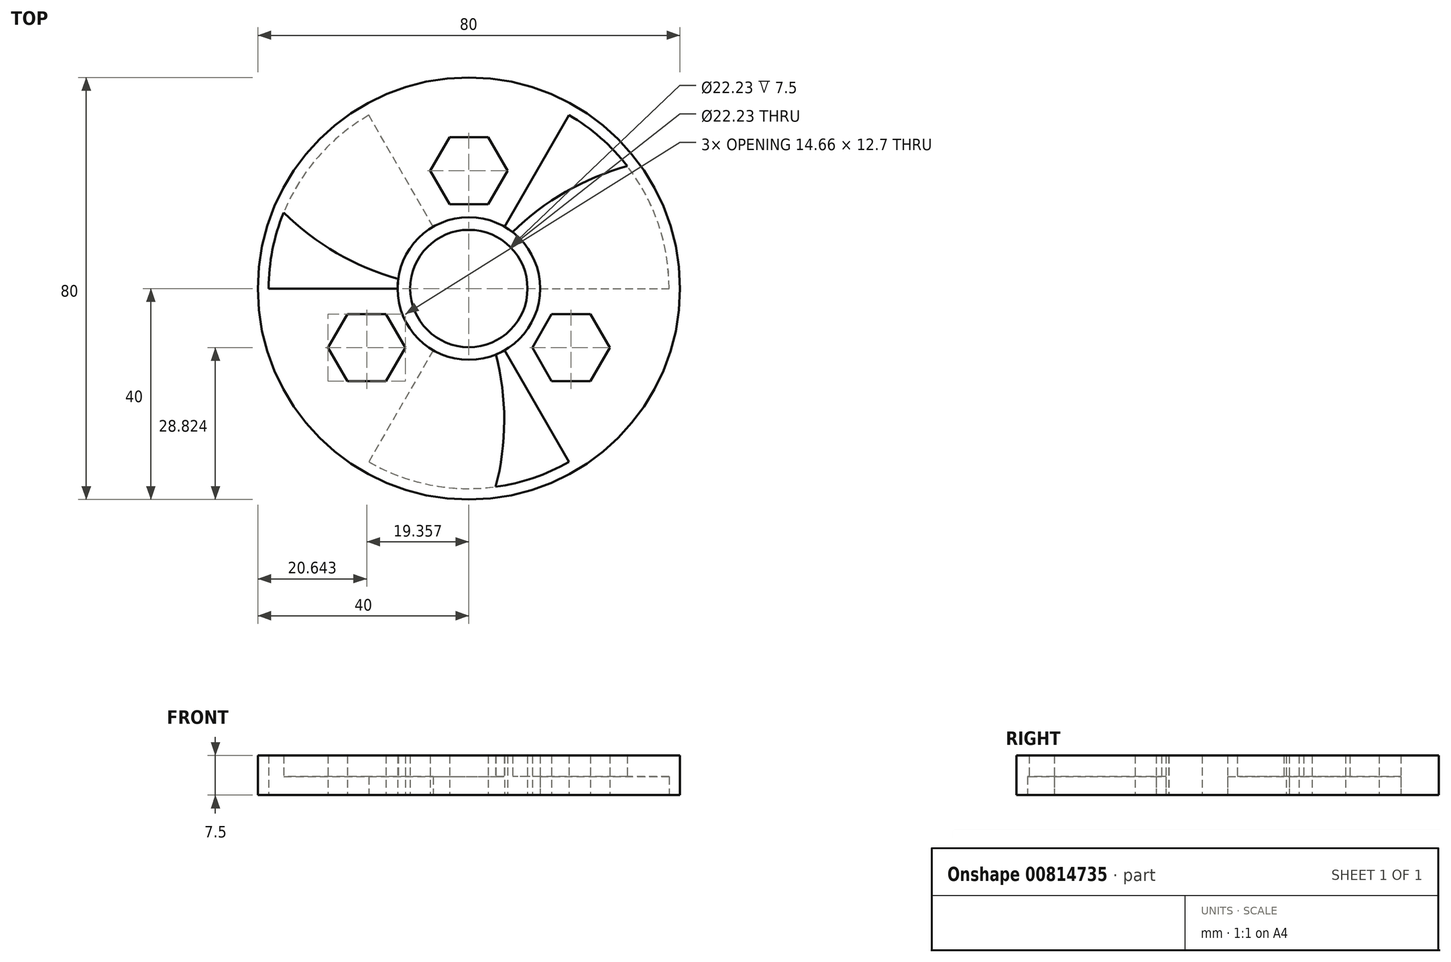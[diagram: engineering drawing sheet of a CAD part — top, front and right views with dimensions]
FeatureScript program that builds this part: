
annotation { "Feature Type Name" : "Feature", "Feature Type Description" : "" }
export const myFeature = defineFeature(function(context is Context, id is Id, definition is map)
    precondition{}
    {
        {
            var Q0;
            Q0=qCreatedBy(makeId("Top.planeOp"),FACE);
            var sketch = newSketch(context, id + "F0", { "sketchPlane" : qUnion([Q0])});
            skCircle(sketch, "E0", {"center": v(0, 0) * mm, "radius": 40 * mm});
            skCircle(sketch, "E1", {"center": v(0, 0) * mm, "radius": 11.11 * mm});
            skCircle(sketch, "E2.cCircle", {"center": v(0, 22.35) * mm, "radius": 6.35 * mm, "construction": true});
            skLineSegment(sketch, "E2.0", {"start": v(3.67, 16) * mm, "end": v(-3.67, 16) * mm});
            skLineSegment(sketch, "E2.1", {"start": v(-3.67, 16) * mm, "end": v(-7.33, 22.35) * mm});
            skLineSegment(sketch, "E2.2", {"start": v(-7.33, 22.35) * mm, "end": v(-3.67, 28.7) * mm});
            skLineSegment(sketch, "E2.3", {"start": v(-3.67, 28.7) * mm, "end": v(3.67, 28.7) * mm});
            skLineSegment(sketch, "E2.4", {"start": v(3.67, 28.7) * mm, "end": v(7.33, 22.35) * mm});
            skLineSegment(sketch, "E2.5", {"start": v(7.33, 22.35) * mm, "end": v(3.67, 16) * mm});
            skPoint(sketch, "E2.0.midPoint", {"position": v(0, 16) * mm});
            skCircle(sketch, "E3.1.0", {"center": v(-19.36, -11.18) * mm, "radius": 6.35 * mm, "construction": true});
            skCircle(sketch, "E3.2.0", {"center": v(19.36, -11.18) * mm, "radius": 6.35 * mm, "construction": true});
            skLineSegment(sketch, "E4.0", {"start": v(-15.7, -17.53) * mm, "end": v(-23.02, -17.53) * mm});
            skLineSegment(sketch, "E4.1", {"start": v(-23.02, -17.53) * mm, "end": v(-26.69, -11.18) * mm});
            skLineSegment(sketch, "E4.2", {"start": v(-26.69, -11.18) * mm, "end": v(-23.02, -4.83) * mm});
            skLineSegment(sketch, "E4.3", {"start": v(-23.02, -4.83) * mm, "end": v(-15.7, -4.83) * mm});
            skLineSegment(sketch, "E4.4", {"start": v(-15.7, -4.83) * mm, "end": v(-12.03, -11.18) * mm});
            skLineSegment(sketch, "E4.5", {"start": v(-12.03, -11.18) * mm, "end": v(-15.7, -17.53) * mm});
            skPoint(sketch, "E4.0.midPoint", {"position": v(-19.36, -17.53) * mm});
            skLineSegment(sketch, "E5.0", {"start": v(23.02, -17.53) * mm, "end": v(15.7, -17.53) * mm});
            skLineSegment(sketch, "E5.1", {"start": v(15.7, -17.53) * mm, "end": v(12.03, -11.18) * mm});
            skLineSegment(sketch, "E5.2", {"start": v(12.03, -11.18) * mm, "end": v(15.7, -4.83) * mm});
            skLineSegment(sketch, "E5.3", {"start": v(15.7, -4.83) * mm, "end": v(23.02, -4.83) * mm});
            skLineSegment(sketch, "E5.4", {"start": v(23.02, -4.83) * mm, "end": v(26.69, -11.18) * mm});
            skLineSegment(sketch, "E5.5", {"start": v(26.69, -11.18) * mm, "end": v(23.02, -17.53) * mm});
            skPoint(sketch, "E5.0.midPoint", {"position": v(19.36, -17.53) * mm});
            skLineSegment(sketch, "E6", {"start": v(0, 0) * mm, "end": v(-20, 34.64) * mm});
            skLineSegment(sketch, "E7", {"start": v(0, 0) * mm, "end": v(-40, 0) * mm});
            skLineSegment(sketch, "E8", {"start": v(0, 0) * mm, "end": v(-19.36, -11.18) * mm});
            skLineSegment(sketch, "E9", {"start": v(0, 0) * mm, "end": v(19.36, -11.18) * mm});
            skLineSegment(sketch, "E10.1.0", {"start": v(0, 0) * mm, "end": v(20, -34.64) * mm});
            skLineSegment(sketch, "E10.1.1", {"start": v(0, 0) * mm, "end": v(-20, -34.64) * mm});
            skLineSegment(sketch, "E10.2.0", {"start": v(0, 0) * mm, "end": v(20, 34.64) * mm});
            skLineSegment(sketch, "E10.2.1", {"start": v(0, 0) * mm, "end": v(40, 0) * mm});
            skArc(sketch, "E11", {"start": v(-36.66, 16) * mm, "mid": v(-20, 4.17) * mm, "end": v(0, 0) * mm});
            skArc(sketch, "E12.1.0", {"start": v(4.47, -39.75) * mm, "mid": v(6.38, -19.4) * mm, "end": v(0, 0) * mm});
            skArc(sketch, "E12.2.0", {"start": v(32.19, 23.75) * mm, "mid": v(13.62, 15.23) * mm, "end": v(0, 0) * mm});
            skCircle(sketch, "E13", {"center": v(0, 0) * mm, "radius": 13.51 * mm});
            skCircle(sketch, "E14", {"center": v(0, 0) * mm, "radius": 37.93 * mm});
            skSolve(sketch);
        }
        {
            var Q0;
            Q0 = qSketchRegion(id + "F0", true);
            var Q1;
            Q1=makeQuery(id+"F0.imprint","IMPRINT",FACE,{"disambiguationData":[TD([[makeQuery(id+"F0.imprint","IMPRINT",EDGE,{"derivedFrom":sQuery(id+"F0.wireOp",EDGE,"E4.0")}),1.0]])]});
            var Q2;
            {var subQ0=sQuery(id+"F0.wireOp",EDGE,"E13");var subQ1=sQuery(id+"F0.wireOp",EDGE,"E10.1.1");var subQ2=makeQuery(id+"F0.imprint","INTERSECT",VERTEX,{"derivedFrom":[subQ1,subQ0]});Q2=makeQuery(id+"F0.imprint","IMPRINT",FACE,{"disambiguationData":[TD([[makeQuery(id+"F0.imprint","IMPRINT",EDGE,{"disambiguationData":[TD([[subQ2,-1.0]])],"derivedFrom":subQ1}),1.0]])]});}
            var Q3;
            {var subQ0=sQuery(id+"F0.wireOp",EDGE,"E13");var subQ1=sQuery(id+"F0.wireOp",EDGE,"E10.1.0");var subQ2=makeQuery(id+"F0.imprint","INTERSECT",VERTEX,{"derivedFrom":[subQ1,subQ0]});Q3=makeQuery(id+"F0.imprint","IMPRINT",FACE,{"disambiguationData":[TD([[makeQuery(id+"F0.imprint","IMPRINT",EDGE,{"disambiguationData":[TD([[subQ2,-1.0]])],"derivedFrom":subQ1}),-1.0]])]});}
            var Q4;
            Q4=makeQuery(id+"F0.imprint","IMPRINT",FACE,{"disambiguationData":[TD([[makeQuery(id+"F0.imprint","IMPRINT",EDGE,{"derivedFrom":sQuery(id+"F0.wireOp",EDGE,"E5.0")}),1.0]])]});
            var Q5;
            {var subQ0=sQuery(id+"F0.wireOp",EDGE,"E8");var subQ1=sQuery(id+"F0.wireOp",EDGE,"E1");var subQ2=makeQuery(id+"F0.imprint","INTERSECT",VERTEX,{"derivedFrom":[subQ1,subQ0]});Q5=makeQuery(id+"F0.imprint","IMPRINT",FACE,{"disambiguationData":[TD([[makeQuery(id+"F0.imprint","IMPRINT",EDGE,{"disambiguationData":[TD([[subQ2,-1.0]])],"derivedFrom":subQ1}),-1.0]])]});}
            var Q6;
            {var subQ0=sQuery(id+"F0.wireOp",EDGE,"E7");var subQ1=sQuery(id+"F0.wireOp",EDGE,"E1");var subQ2=makeQuery(id+"F0.imprint","INTERSECT",VERTEX,{"derivedFrom":[subQ1,subQ0]});Q6=makeQuery(id+"F0.imprint","IMPRINT",FACE,{"disambiguationData":[TD([[makeQuery(id+"F0.imprint","IMPRINT",EDGE,{"disambiguationData":[TD([[subQ2,-1.0]])],"derivedFrom":subQ1}),-1.0]])]});}
            var Q7;
            {var subQ0=sQuery(id+"F0.wireOp",EDGE,"E6");var subQ1=sQuery(id+"F0.wireOp",EDGE,"E1");var subQ2=makeQuery(id+"F0.imprint","INTERSECT",VERTEX,{"derivedFrom":[subQ1,subQ0]});Q7=makeQuery(id+"F0.imprint","IMPRINT",FACE,{"disambiguationData":[TD([[makeQuery(id+"F0.imprint","IMPRINT",EDGE,{"disambiguationData":[TD([[subQ2,-1.0]])],"derivedFrom":subQ1}),-1.0]])]});}
            var Q8;
            {var subQ0=sQuery(id+"F0.wireOp",EDGE,"E13");var subQ1=sQuery(id+"F0.wireOp",EDGE,"E7");var subQ2=makeQuery(id+"F0.imprint","INTERSECT",VERTEX,{"derivedFrom":[subQ1,subQ0]});Q8=makeQuery(id+"F0.imprint","IMPRINT",FACE,{"disambiguationData":[TD([[makeQuery(id+"F0.imprint","IMPRINT",EDGE,{"disambiguationData":[TD([[subQ2,-1.0]])],"derivedFrom":subQ1}),-1.0]])]});}
            var Q9;
            {var subQ0=sQuery(id+"F0.wireOp",EDGE,"E13");var subQ1=sQuery(id+"F0.wireOp",EDGE,"E6");var subQ2=makeQuery(id+"F0.imprint","INTERSECT",VERTEX,{"derivedFrom":[subQ1,subQ0]});Q9=makeQuery(id+"F0.imprint","IMPRINT",FACE,{"disambiguationData":[TD([[makeQuery(id+"F0.imprint","IMPRINT",EDGE,{"disambiguationData":[TD([[subQ2,-1.0]])],"derivedFrom":subQ1}),1.0]])]});}
            var Q10;
            Q10=makeQuery(id+"F0.imprint","IMPRINT",FACE,{"disambiguationData":[TD([[makeQuery(id+"F0.imprint","IMPRINT",EDGE,{"derivedFrom":sQuery(id+"F0.wireOp",EDGE,"E2.0")}),1.0]])]});
            var Q11;
            {var subQ0=sQuery(id+"F0.wireOp",EDGE,"E10.2.0");var subQ1=sQuery(id+"F0.wireOp",EDGE,"E1");var subQ2=makeQuery(id+"F0.imprint","INTERSECT",VERTEX,{"derivedFrom":[subQ1,subQ0]});Q11=makeQuery(id+"F0.imprint","IMPRINT",FACE,{"disambiguationData":[TD([[makeQuery(id+"F0.imprint","IMPRINT",EDGE,{"disambiguationData":[TD([[subQ2,-1.0]])],"derivedFrom":subQ1}),-1.0]])]});}
            var Q12;
            {var subQ0=sQuery(id+"F0.wireOp",EDGE,"E11");var subQ1=sQuery(id+"F0.wireOp",EDGE,"E1");var subQ2=makeQuery(id+"F0.imprint","INTERSECT",VERTEX,{"derivedFrom":[subQ1,subQ0]});Q12=makeQuery(id+"F0.imprint","IMPRINT",FACE,{"disambiguationData":[TD([[makeQuery(id+"F0.imprint","IMPRINT",EDGE,{"disambiguationData":[TD([[subQ2,-1.0]])],"derivedFrom":subQ1}),-1.0]])]});}
            var Q13;
            {var subQ0=sQuery(id+"F0.wireOp",EDGE,"E12.2.0");var subQ1=sQuery(id+"F0.wireOp",EDGE,"E1");var subQ2=makeQuery(id+"F0.imprint","INTERSECT",VERTEX,{"derivedFrom":[subQ1,subQ0]});Q13=makeQuery(id+"F0.imprint","IMPRINT",FACE,{"disambiguationData":[TD([[makeQuery(id+"F0.imprint","IMPRINT",EDGE,{"disambiguationData":[TD([[subQ2,1.0]])],"derivedFrom":subQ1}),-1.0]])]});}
            var Q14;
            {var subQ0=sQuery(id+"F0.wireOp",EDGE,"E12.2.0");var subQ1=sQuery(id+"F0.wireOp",EDGE,"E1");var subQ2=makeQuery(id+"F0.imprint","INTERSECT",VERTEX,{"derivedFrom":[subQ1,subQ0]});Q14=makeQuery(id+"F0.imprint","IMPRINT",FACE,{"disambiguationData":[TD([[makeQuery(id+"F0.imprint","IMPRINT",EDGE,{"disambiguationData":[TD([[subQ2,-1.0]])],"derivedFrom":subQ1}),-1.0]])]});}
            var Q15;
            {var subQ0=sQuery(id+"F0.wireOp",EDGE,"E10.1.0");var subQ1=sQuery(id+"F0.wireOp",EDGE,"E1");var subQ2=makeQuery(id+"F0.imprint","INTERSECT",VERTEX,{"derivedFrom":[subQ1,subQ0]});Q15=makeQuery(id+"F0.imprint","IMPRINT",FACE,{"disambiguationData":[TD([[makeQuery(id+"F0.imprint","IMPRINT",EDGE,{"disambiguationData":[TD([[subQ2,-1.0]])],"derivedFrom":subQ1}),-1.0]])]});}
            var Q16;
            {var subQ0=sQuery(id+"F0.wireOp",EDGE,"E10.2.1");var subQ1=sQuery(id+"F0.wireOp",EDGE,"E1");var subQ2=makeQuery(id+"F0.imprint","INTERSECT",VERTEX,{"derivedFrom":[subQ1,subQ0]});Q16=makeQuery(id+"F0.imprint","IMPRINT",FACE,{"disambiguationData":[TD([[makeQuery(id+"F0.imprint","IMPRINT",EDGE,{"disambiguationData":[TD([[subQ2,1.0]])],"derivedFrom":subQ1}),-1.0]])]});}
            var Q17;
            {var subQ0=sQuery(id+"F0.wireOp",EDGE,"E12.1.0");var subQ1=sQuery(id+"F0.wireOp",EDGE,"E1");var subQ2=makeQuery(id+"F0.imprint","INTERSECT",VERTEX,{"derivedFrom":[subQ1,subQ0]});Q17=makeQuery(id+"F0.imprint","IMPRINT",FACE,{"disambiguationData":[TD([[makeQuery(id+"F0.imprint","IMPRINT",EDGE,{"disambiguationData":[TD([[subQ2,-1.0]])],"derivedFrom":subQ1}),-1.0]])]});}
            var Q18;
            {var subQ0=sQuery(id+"F0.wireOp",EDGE,"E10.1.1");var subQ1=sQuery(id+"F0.wireOp",EDGE,"E1");var subQ2=makeQuery(id+"F0.imprint","INTERSECT",VERTEX,{"derivedFrom":[subQ1,subQ0]});Q18=makeQuery(id+"F0.imprint","IMPRINT",FACE,{"disambiguationData":[TD([[makeQuery(id+"F0.imprint","IMPRINT",EDGE,{"disambiguationData":[TD([[subQ2,-1.0]])],"derivedFrom":subQ1}),-1.0]])]});}
            var Q19;
            {var subQ0=sQuery(id+"F0.wireOp",EDGE,"E13");var subQ1=sQuery(id+"F0.wireOp",EDGE,"E10.2.1");var subQ2=makeQuery(id+"F0.imprint","INTERSECT",VERTEX,{"derivedFrom":[subQ1,subQ0]});Q19=makeQuery(id+"F0.imprint","IMPRINT",FACE,{"disambiguationData":[TD([[makeQuery(id+"F0.imprint","IMPRINT",EDGE,{"disambiguationData":[TD([[subQ2,-1.0]])],"derivedFrom":subQ1}),1.0]])]});}
            var Q20;
            {var subQ0=sQuery(id+"F0.wireOp",EDGE,"E13");var subQ1=sQuery(id+"F0.wireOp",EDGE,"E10.2.0");var subQ2=makeQuery(id+"F0.imprint","INTERSECT",VERTEX,{"derivedFrom":[subQ1,subQ0]});Q20=makeQuery(id+"F0.imprint","IMPRINT",FACE,{"disambiguationData":[TD([[makeQuery(id+"F0.imprint","IMPRINT",EDGE,{"disambiguationData":[TD([[subQ2,-1.0]])],"derivedFrom":subQ1}),-1.0]])]});}
            extrude(context, id + "F1", {"entities" : qUnion([Q0, Q1, Q2, Q3, Q4, Q5, Q6, Q7, Q8, Q9, Q10, Q11, Q12, Q13, Q14, Q15, Q16, Q17, Q18, Q19, Q20]), "depth" : 7.5 * mm, "offsetDistance" : 25 * mm});
        }
        {
            var Q0;
            {var subQ0=sQuery(id+"F0.wireOp",EDGE,"E6");var subQ1=sQuery(id+"F0.wireOp",EDGE,"E0");var subQ2=makeQuery(id+"F0.imprint","INTERSECT",VERTEX,{"derivedFrom":[subQ1,subQ0]});Q0=makeQuery(id+"F0.imprint","IMPRINT",FACE,{"disambiguationData":[TD([[makeQuery(id+"F0.imprint","IMPRINT",EDGE,{"disambiguationData":[TD([[subQ2,-1.0]])],"derivedFrom":subQ1}),1.0]])]});}
            var Q1;
            {var subQ0=sQuery(id+"F0.wireOp",EDGE,"E10.1.1");var subQ1=sQuery(id+"F0.wireOp",EDGE,"E0");var subQ2=makeQuery(id+"F0.imprint","INTERSECT",VERTEX,{"derivedFrom":[subQ1,subQ0]});Q1=makeQuery(id+"F0.imprint","IMPRINT",FACE,{"disambiguationData":[TD([[makeQuery(id+"F0.imprint","IMPRINT",EDGE,{"disambiguationData":[TD([[subQ2,-1.0]])],"derivedFrom":subQ1}),1.0]])]});}
            var Q2;
            {var subQ0=sQuery(id+"F0.wireOp",EDGE,"E10.2.1");var subQ1=sQuery(id+"F0.wireOp",EDGE,"E0");var subQ2=makeQuery(id+"F0.imprint","INTERSECT",VERTEX,{"derivedFrom":[subQ1,subQ0]});Q2=makeQuery(id+"F0.imprint","IMPRINT",FACE,{"disambiguationData":[TD([[makeQuery(id+"F0.imprint","IMPRINT",EDGE,{"disambiguationData":[TD([[subQ2,-1.0]])],"derivedFrom":subQ1}),1.0]])]});}
            extrude(context, id + "F2", {"entities" : qUnion([Q0, Q1, Q2]), "operationType" : NewBodyOperationType.REMOVE, "depth" : 3.25 * mm, "offsetDistance" : 25 * mm});
        }
        {
            var Q0;
            {var subQ0=sQuery(id+"F0.wireOp",EDGE,"E7");var subQ1=sQuery(id+"F0.wireOp",EDGE,"E0");var subQ2=makeQuery(id+"F0.imprint","INTERSECT",VERTEX,{"derivedFrom":[subQ1,subQ0]});Q0=makeQuery(id+"F0.imprint","IMPRINT",FACE,{"disambiguationData":[TD([[makeQuery(id+"F0.imprint","IMPRINT",EDGE,{"disambiguationData":[TD([[subQ2,1.0]])],"derivedFrom":subQ1}),1.0]])]});}
            var Q1;
            {var subQ0=sQuery(id+"F0.wireOp",EDGE,"E10.2.0");var subQ1=sQuery(id+"F0.wireOp",EDGE,"E0");var subQ2=makeQuery(id+"F0.imprint","INTERSECT",VERTEX,{"derivedFrom":[subQ1,subQ0]});Q1=makeQuery(id+"F0.imprint","IMPRINT",FACE,{"disambiguationData":[TD([[makeQuery(id+"F0.imprint","IMPRINT",EDGE,{"disambiguationData":[TD([[subQ2,1.0]])],"derivedFrom":subQ1}),1.0]])]});}
            var Q2;
            {var subQ0=sQuery(id+"F0.wireOp",EDGE,"E10.1.0");var subQ1=sQuery(id+"F0.wireOp",EDGE,"E0");var subQ2=makeQuery(id+"F0.imprint","INTERSECT",VERTEX,{"derivedFrom":[subQ1,subQ0]});Q2=makeQuery(id+"F0.imprint","IMPRINT",FACE,{"disambiguationData":[TD([[makeQuery(id+"F0.imprint","IMPRINT",EDGE,{"disambiguationData":[TD([[subQ2,1.0]])],"derivedFrom":subQ1}),1.0]])]});}
            extrude(context, id + "F3", {"entities" : qUnion([Q0, Q1, Q2]), "operationType" : NewBodyOperationType.REMOVE, "depth" : 25 * mm, "offsetDistance" : 25 * mm});
        }
        {
            var Q0;
            {var subQ0=sQuery(id+"F0.wireOp",EDGE,"E7");var subQ1=sQuery(id+"F0.wireOp",EDGE,"E1");var subQ2=makeQuery(id+"F0.imprint","INTERSECT",VERTEX,{"derivedFrom":[subQ1,subQ0]});Q0=makeQuery(id+"F0.imprint","IMPRINT",FACE,{"disambiguationData":[TD([[makeQuery(id+"F0.imprint","IMPRINT",EDGE,{"disambiguationData":[TD([[subQ2,-1.0]])],"derivedFrom":subQ1}),-1.0]])]});}
            var Q1;
            {var subQ0=sQuery(id+"F0.wireOp",EDGE,"E11");var subQ1=sQuery(id+"F0.wireOp",EDGE,"E1");var subQ2=makeQuery(id+"F0.imprint","INTERSECT",VERTEX,{"derivedFrom":[subQ1,subQ0]});Q1=makeQuery(id+"F0.imprint","IMPRINT",FACE,{"disambiguationData":[TD([[makeQuery(id+"F0.imprint","IMPRINT",EDGE,{"disambiguationData":[TD([[subQ2,-1.0]])],"derivedFrom":subQ1}),-1.0]])]});}
            var Q2;
            {var subQ0=sQuery(id+"F0.wireOp",EDGE,"E6");var subQ1=sQuery(id+"F0.wireOp",EDGE,"E1");var subQ2=makeQuery(id+"F0.imprint","INTERSECT",VERTEX,{"derivedFrom":[subQ1,subQ0]});Q2=makeQuery(id+"F0.imprint","IMPRINT",FACE,{"disambiguationData":[TD([[makeQuery(id+"F0.imprint","IMPRINT",EDGE,{"disambiguationData":[TD([[subQ2,-1.0]])],"derivedFrom":subQ1}),-1.0]])]});}
            var Q3;
            {var subQ0=sQuery(id+"F0.wireOp",EDGE,"E10.2.0");var subQ1=sQuery(id+"F0.wireOp",EDGE,"E1");var subQ2=makeQuery(id+"F0.imprint","INTERSECT",VERTEX,{"derivedFrom":[subQ1,subQ0]});Q3=makeQuery(id+"F0.imprint","IMPRINT",FACE,{"disambiguationData":[TD([[makeQuery(id+"F0.imprint","IMPRINT",EDGE,{"disambiguationData":[TD([[subQ2,-1.0]])],"derivedFrom":subQ1}),-1.0]])]});}
            var Q4;
            {var subQ0=sQuery(id+"F0.wireOp",EDGE,"E12.2.0");var subQ1=sQuery(id+"F0.wireOp",EDGE,"E1");var subQ2=makeQuery(id+"F0.imprint","INTERSECT",VERTEX,{"derivedFrom":[subQ1,subQ0]});Q4=makeQuery(id+"F0.imprint","IMPRINT",FACE,{"disambiguationData":[TD([[makeQuery(id+"F0.imprint","IMPRINT",EDGE,{"disambiguationData":[TD([[subQ2,-1.0]])],"derivedFrom":subQ1}),-1.0]])]});}
            var Q5;
            {var subQ0=sQuery(id+"F0.wireOp",EDGE,"E12.2.0");var subQ1=sQuery(id+"F0.wireOp",EDGE,"E1");var subQ2=makeQuery(id+"F0.imprint","INTERSECT",VERTEX,{"derivedFrom":[subQ1,subQ0]});Q5=makeQuery(id+"F0.imprint","IMPRINT",FACE,{"disambiguationData":[TD([[makeQuery(id+"F0.imprint","IMPRINT",EDGE,{"disambiguationData":[TD([[subQ2,1.0]])],"derivedFrom":subQ1}),-1.0]])]});}
            var Q6;
            {var subQ0=sQuery(id+"F0.wireOp",EDGE,"E10.2.1");var subQ1=sQuery(id+"F0.wireOp",EDGE,"E1");var subQ2=makeQuery(id+"F0.imprint","INTERSECT",VERTEX,{"derivedFrom":[subQ1,subQ0]});Q6=makeQuery(id+"F0.imprint","IMPRINT",FACE,{"disambiguationData":[TD([[makeQuery(id+"F0.imprint","IMPRINT",EDGE,{"disambiguationData":[TD([[subQ2,1.0]])],"derivedFrom":subQ1}),-1.0]])]});}
            var Q7;
            {var subQ0=sQuery(id+"F0.wireOp",EDGE,"E12.1.0");var subQ1=sQuery(id+"F0.wireOp",EDGE,"E1");var subQ2=makeQuery(id+"F0.imprint","INTERSECT",VERTEX,{"derivedFrom":[subQ1,subQ0]});Q7=makeQuery(id+"F0.imprint","IMPRINT",FACE,{"disambiguationData":[TD([[makeQuery(id+"F0.imprint","IMPRINT",EDGE,{"disambiguationData":[TD([[subQ2,-1.0]])],"derivedFrom":subQ1}),-1.0]])]});}
            var Q8;
            {var subQ0=sQuery(id+"F0.wireOp",EDGE,"E10.1.0");var subQ1=sQuery(id+"F0.wireOp",EDGE,"E1");var subQ2=makeQuery(id+"F0.imprint","INTERSECT",VERTEX,{"derivedFrom":[subQ1,subQ0]});Q8=makeQuery(id+"F0.imprint","IMPRINT",FACE,{"disambiguationData":[TD([[makeQuery(id+"F0.imprint","IMPRINT",EDGE,{"disambiguationData":[TD([[subQ2,-1.0]])],"derivedFrom":subQ1}),-1.0]])]});}
            var Q9;
            {var subQ0=sQuery(id+"F0.wireOp",EDGE,"E10.1.1");var subQ1=sQuery(id+"F0.wireOp",EDGE,"E1");var subQ2=makeQuery(id+"F0.imprint","INTERSECT",VERTEX,{"derivedFrom":[subQ1,subQ0]});Q9=makeQuery(id+"F0.imprint","IMPRINT",FACE,{"disambiguationData":[TD([[makeQuery(id+"F0.imprint","IMPRINT",EDGE,{"disambiguationData":[TD([[subQ2,-1.0]])],"derivedFrom":subQ1}),-1.0]])]});}
            var Q10;
            {var subQ0=sQuery(id+"F0.wireOp",EDGE,"E8");var subQ1=sQuery(id+"F0.wireOp",EDGE,"E1");var subQ2=makeQuery(id+"F0.imprint","INTERSECT",VERTEX,{"derivedFrom":[subQ1,subQ0]});Q10=makeQuery(id+"F0.imprint","IMPRINT",FACE,{"disambiguationData":[TD([[makeQuery(id+"F0.imprint","IMPRINT",EDGE,{"disambiguationData":[TD([[subQ2,-1.0]])],"derivedFrom":subQ1}),-1.0]])]});}
            extrude(context, id + "F4", {"entities" : qUnion([Q0, Q1, Q2, Q3, Q4, Q5, Q6, Q7, Q8, Q9, Q10]), "depth" : 7.5 * mm, "offsetDistance" : 25 * mm});
        }
        {
            var Q0;
            {var subQ0=sQuery(id+"F0.wireOp",EDGE,"E7");var subQ1=sQuery(id+"F0.wireOp",EDGE,"E0");var subQ2=makeQuery(id+"F0.imprint","INTERSECT",VERTEX,{"derivedFrom":[subQ1,subQ0]});Q0=makeQuery(id+"F0.imprint","IMPRINT",FACE,{"disambiguationData":[TD([[makeQuery(id+"F0.imprint","IMPRINT",EDGE,{"disambiguationData":[TD([[subQ2,1.0]])],"derivedFrom":subQ1}),1.0]])]});}
            var Q1;
            {var subQ0=sQuery(id+"F0.wireOp",EDGE,"E6");var subQ1=sQuery(id+"F0.wireOp",EDGE,"E0");var subQ2=makeQuery(id+"F0.imprint","INTERSECT",VERTEX,{"derivedFrom":[subQ1,subQ0]});Q1=makeQuery(id+"F0.imprint","IMPRINT",FACE,{"disambiguationData":[TD([[makeQuery(id+"F0.imprint","IMPRINT",EDGE,{"disambiguationData":[TD([[subQ2,-1.0]])],"derivedFrom":subQ1}),1.0]])]});}
            var Q2;
            {var subQ0=sQuery(id+"F0.wireOp",EDGE,"E7");var subQ1=sQuery(id+"F0.wireOp",EDGE,"E0");var subQ2=makeQuery(id+"F0.imprint","INTERSECT",VERTEX,{"derivedFrom":[subQ1,subQ0]});Q2=makeQuery(id+"F0.imprint","IMPRINT",FACE,{"disambiguationData":[TD([[makeQuery(id+"F0.imprint","IMPRINT",EDGE,{"disambiguationData":[TD([[subQ2,-1.0]])],"derivedFrom":subQ1}),1.0]])]});}
            var Q3;
            {var subQ0=sQuery(id+"F0.wireOp",EDGE,"E10.1.1");var subQ1=sQuery(id+"F0.wireOp",EDGE,"E0");var subQ2=makeQuery(id+"F0.imprint","INTERSECT",VERTEX,{"derivedFrom":[subQ1,subQ0]});Q3=makeQuery(id+"F0.imprint","IMPRINT",FACE,{"disambiguationData":[TD([[makeQuery(id+"F0.imprint","IMPRINT",EDGE,{"disambiguationData":[TD([[subQ2,-1.0]])],"derivedFrom":subQ1}),1.0]])]});}
            var Q4;
            {var subQ0=sQuery(id+"F0.wireOp",EDGE,"E10.1.0");var subQ1=sQuery(id+"F0.wireOp",EDGE,"E0");var subQ2=makeQuery(id+"F0.imprint","INTERSECT",VERTEX,{"derivedFrom":[subQ1,subQ0]});Q4=makeQuery(id+"F0.imprint","IMPRINT",FACE,{"disambiguationData":[TD([[makeQuery(id+"F0.imprint","IMPRINT",EDGE,{"disambiguationData":[TD([[subQ2,1.0]])],"derivedFrom":subQ1}),1.0]])]});}
            var Q5;
            {var subQ0=sQuery(id+"F0.wireOp",EDGE,"E10.1.0");var subQ1=sQuery(id+"F0.wireOp",EDGE,"E0");var subQ2=makeQuery(id+"F0.imprint","INTERSECT",VERTEX,{"derivedFrom":[subQ1,subQ0]});Q5=makeQuery(id+"F0.imprint","IMPRINT",FACE,{"disambiguationData":[TD([[makeQuery(id+"F0.imprint","IMPRINT",EDGE,{"disambiguationData":[TD([[subQ2,-1.0]])],"derivedFrom":subQ1}),1.0]])]});}
            var Q6;
            {var subQ0=sQuery(id+"F0.wireOp",EDGE,"E10.2.1");var subQ1=sQuery(id+"F0.wireOp",EDGE,"E0");var subQ2=makeQuery(id+"F0.imprint","INTERSECT",VERTEX,{"derivedFrom":[subQ1,subQ0]});Q6=makeQuery(id+"F0.imprint","IMPRINT",FACE,{"disambiguationData":[TD([[makeQuery(id+"F0.imprint","IMPRINT",EDGE,{"disambiguationData":[TD([[subQ2,-1.0]])],"derivedFrom":subQ1}),1.0]])]});}
            var Q7;
            {var subQ0=sQuery(id+"F0.wireOp",EDGE,"E10.2.0");var subQ1=sQuery(id+"F0.wireOp",EDGE,"E0");var subQ2=makeQuery(id+"F0.imprint","INTERSECT",VERTEX,{"derivedFrom":[subQ1,subQ0]});Q7=makeQuery(id+"F0.imprint","IMPRINT",FACE,{"disambiguationData":[TD([[makeQuery(id+"F0.imprint","IMPRINT",EDGE,{"disambiguationData":[TD([[subQ2,1.0]])],"derivedFrom":subQ1}),1.0]])]});}
            var Q8;
            {var subQ0=sQuery(id+"F0.wireOp",EDGE,"E6");var subQ1=sQuery(id+"F0.wireOp",EDGE,"E0");var subQ2=makeQuery(id+"F0.imprint","INTERSECT",VERTEX,{"derivedFrom":[subQ1,subQ0]});Q8=makeQuery(id+"F0.imprint","IMPRINT",FACE,{"disambiguationData":[TD([[makeQuery(id+"F0.imprint","IMPRINT",EDGE,{"disambiguationData":[TD([[subQ2,1.0]])],"derivedFrom":subQ1}),1.0]])]});}
            extrude(context, id + "F5", {"entities" : qUnion([Q0, Q1, Q2, Q3, Q4, Q5, Q6, Q7, Q8]), "operationType" : NewBodyOperationType.ADD, "depth" : 7.5 * mm, "offsetDistance" : 25 * mm});
        }
        {
            var Q0;
            {var subQ0=sQuery(id+"F0.wireOp",EDGE,"E13");var subQ1=sQuery(id+"F0.wireOp",EDGE,"E10.1.0");var subQ2=makeQuery(id+"F0.imprint","INTERSECT",VERTEX,{"derivedFrom":[subQ1,subQ0]});Q0=makeQuery(id+"F0.imprint","IMPRINT",FACE,{"disambiguationData":[TD([[makeQuery(id+"F0.imprint","IMPRINT",EDGE,{"disambiguationData":[TD([[subQ2,-1.0]])],"derivedFrom":subQ1}),-1.0]])]});}
            var Q1;
            {var subQ0=sQuery(id+"F0.wireOp",EDGE,"E13");var subQ1=sQuery(id+"F0.wireOp",EDGE,"E7");var subQ2=makeQuery(id+"F0.imprint","INTERSECT",VERTEX,{"derivedFrom":[subQ1,subQ0]});Q1=makeQuery(id+"F0.imprint","IMPRINT",FACE,{"disambiguationData":[TD([[makeQuery(id+"F0.imprint","IMPRINT",EDGE,{"disambiguationData":[TD([[subQ2,-1.0]])],"derivedFrom":subQ1}),-1.0]])]});}
            var Q2;
            {var subQ0=sQuery(id+"F0.wireOp",EDGE,"E13");var subQ1=sQuery(id+"F0.wireOp",EDGE,"E10.2.0");var subQ2=makeQuery(id+"F0.imprint","INTERSECT",VERTEX,{"derivedFrom":[subQ1,subQ0]});Q2=makeQuery(id+"F0.imprint","IMPRINT",FACE,{"disambiguationData":[TD([[makeQuery(id+"F0.imprint","IMPRINT",EDGE,{"disambiguationData":[TD([[subQ2,-1.0]])],"derivedFrom":subQ1}),-1.0]])]});}
            extrude(context, id + "F6", {"entities" : qUnion([Q0, Q1, Q2]), "operationType" : NewBodyOperationType.REMOVE, "depth" : 25 * mm, "offsetDistance" : 25 * mm});
        }
        {
            var Q0;
            {var subQ0=sQuery(id+"F0.wireOp",EDGE,"E13");var subQ1=sQuery(id+"F0.wireOp",EDGE,"E6");var subQ2=makeQuery(id+"F0.imprint","INTERSECT",VERTEX,{"derivedFrom":[subQ1,subQ0]});Q0=makeQuery(id+"F0.imprint","IMPRINT",FACE,{"disambiguationData":[TD([[makeQuery(id+"F0.imprint","IMPRINT",EDGE,{"disambiguationData":[TD([[subQ2,-1.0]])],"derivedFrom":subQ1}),1.0]])]});}
            var Q1;
            {var subQ0=sQuery(id+"F0.wireOp",EDGE,"E13");var subQ1=sQuery(id+"F0.wireOp",EDGE,"E10.2.1");var subQ2=makeQuery(id+"F0.imprint","INTERSECT",VERTEX,{"derivedFrom":[subQ1,subQ0]});Q1=makeQuery(id+"F0.imprint","IMPRINT",FACE,{"disambiguationData":[TD([[makeQuery(id+"F0.imprint","IMPRINT",EDGE,{"disambiguationData":[TD([[subQ2,-1.0]])],"derivedFrom":subQ1}),1.0]])]});}
            var Q2;
            {var subQ0=sQuery(id+"F0.wireOp",EDGE,"E13");var subQ1=sQuery(id+"F0.wireOp",EDGE,"E10.1.1");var subQ2=makeQuery(id+"F0.imprint","INTERSECT",VERTEX,{"derivedFrom":[subQ1,subQ0]});Q2=makeQuery(id+"F0.imprint","IMPRINT",FACE,{"disambiguationData":[TD([[makeQuery(id+"F0.imprint","IMPRINT",EDGE,{"disambiguationData":[TD([[subQ2,-1.0]])],"derivedFrom":subQ1}),1.0]])]});}
            extrude(context, id + "F7", {"entities" : qUnion([Q0, Q1, Q2]), "operationType" : NewBodyOperationType.REMOVE, "oppositeDirection" : true, "depth" : -3.5 * mm, "offsetDistance" : 25 * mm});
        }
    });
